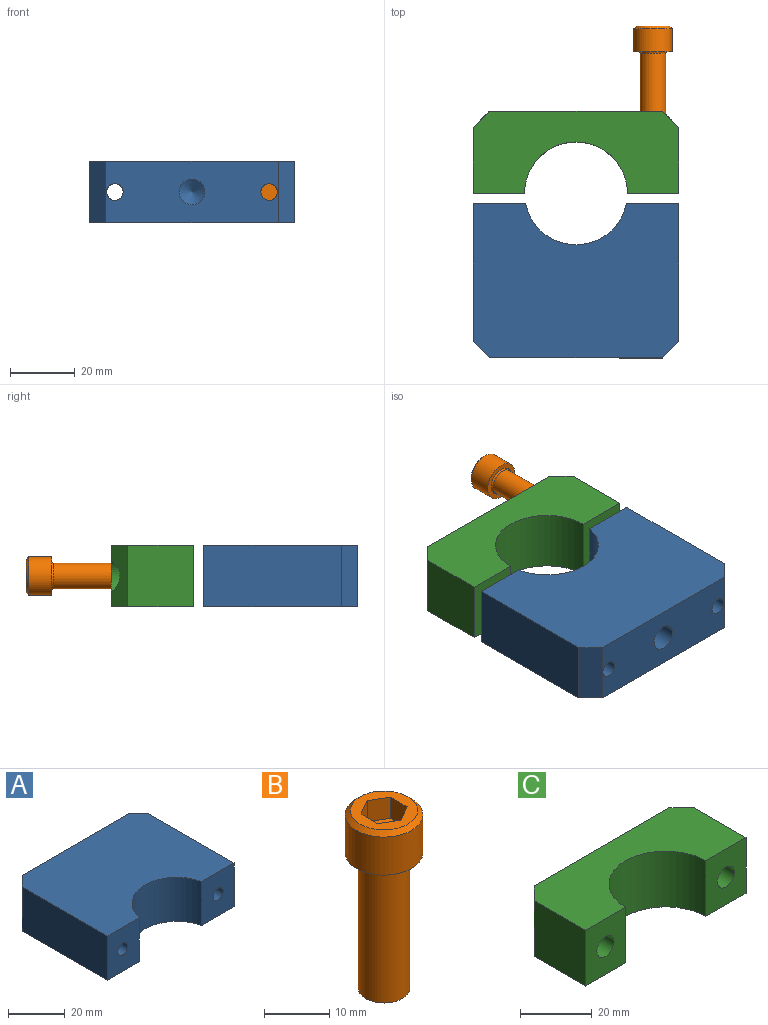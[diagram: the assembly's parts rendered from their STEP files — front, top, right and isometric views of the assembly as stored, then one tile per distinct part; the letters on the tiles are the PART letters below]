
ASSEMBLY  parts=3 mates=3
PART A: 14 faces, bbox 63.5x47.6x19.1 mm
  f0: plane 42.55x19.05mm, normal (1,0,0), area 810.5mm2, adj f3,f4,f9,f11
  f1: plane 42.55x19.05mm, normal (-1,0,0), area 810.5mm2, adj f3,f4,f8,f10
  f2: cylinder r=15.88mm len=31.11mm, axis (0,0,-1), area 828.3mm2, adj f3,f4,f10,f11
  f3: plane 63.5x47.63mm, normal (0,0,1), area 2702.6mm2, adj f0,f1,f2,f7,f8,f9,f10,f11
  f4: plane 63.5x47.63mm, normal (0,0,-1), area 2702.6mm2, adj f0,f1,f2,f7,f8,f9,f10,f11
  f5: cylinder r=2.55mm len=47.63mm, axis (0,1,0), area 763.9mm2, adj f7,f11
  f6: cylinder r=2.55mm len=47.63mm, axis (0,1,0), area 763.9mm2, adj f7,f10
  f7: plane 53.34x19.05mm, normal (0,1,0), area 925.7mm2, adj f3,f4,f5,f6,f8,f9,f12
  f8: plane 19.05x5.08mm, normal (-0.71,0.71,0), area 136.9mm2, adj f1,f3,f4,f7
  f9: plane 19.05x5.08mm, normal (0.71,0.71,0), area 136.9mm2, adj f0,f3,f4,f7
  f10: plane 19.05x16.2mm, normal (0,-1,0), area 288.1mm2, adj f1,f2,f3,f4,f6
  f11: plane 19.05x16.2mm, normal (0,-1,0), area 288.1mm2, adj f0,f2,f3,f4,f5
  f12: cylinder r=3.97mm len=17.48mm, axis (0,1,0), area 435.8mm2, adj f7,f13
  f13: cone r=0mm half-angle=59deg, axis (0,1,0), area 57.7mm2, adj f12
PART B: 14 faces, bbox 11.9x11.9x33.3 mm
  f0: cylinder r=3.97mm len=24.97mm, axis (0,0,-1), area 622.6mm2, adj f1,f5
  f1: plane 7.94x7.94mm, normal (0,0,-1), area 49.5mm2, adj f0
  f2: plane 11.91x11.91mm, normal (0,0,-1), area 50.6mm2, adj f3,f5
  f3: cylinder r=5.96mm len=11.91mm, axis (0,0,-1), area 267.3mm2, adj f2,f13
  f4: plane 10.32x10.32mm, normal (0,0,1), area 48.8mm2, adj f6,f7,f8,f9,f10,f11,f13
  f5: torus R=4.4mm, axis (0,0,1), area 17.6mm2, adj f0,f2
  f6: plane 3.97x3.18mm, normal (0.5,-0.87,0), area 14.6mm2, adj f4,f7,f11,f12
  f7: plane 3.97x3.18mm, normal (-0.5,-0.87,0), area 14.6mm2, adj f4,f6,f8,f12
  f8: plane 3.97x3.67mm, normal (-1,0,0), area 14.6mm2, adj f4,f7,f9,f12
  f9: plane 3.97x3.18mm, normal (-0.5,0.87,0), area 14.6mm2, adj f4,f8,f10,f12
  f10: plane 3.97x3.18mm, normal (0.5,0.87,0), area 14.6mm2, adj f4,f9,f11,f12
  f11: plane 3.97x3.67mm, normal (1,0,0), area 14.6mm2, adj f4,f6,f10,f12
  f12: plane 7.33x6.35mm, normal (0,0,1), area 34.9mm2, adj f6,f7,f8,f9,f10,f11
  f13: cone r=5.16mm half-angle=45deg, axis (0,0,-1), area 39.2mm2, adj f3,f4
PART C: 16 faces, bbox 63.5x25.4x19.1 mm
  f0: plane 19.05x15.88mm, normal (0,-1,0), area 266.6mm2, adj f1,f5,f6,f7,f8
  f1: plane 20.32x19.05mm, normal (1,0,0), area 387.1mm2, adj f0,f6,f7,f15
  f2: plane 53.34x19.05mm, normal (0,1,0), area 858.6mm2, adj f6,f7,f10,f13,f14,f15
  f3: plane 20.32x19.05mm, normal (-1,0,0), area 387.1mm2, adj f4,f6,f7,f14
  f4: plane 19.05x15.88mm, normal (0,-1,0), area 266.6mm2, adj f3,f5,f6,f7,f11
  f5: cylinder r=15.88mm len=31.75mm, axis (0,0,-1), area 950.1mm2, adj f0,f4,f6,f7
  f6: plane 63.5x25.4mm, normal (0,0,1), area 1191.2mm2, adj f0,f1,f2,f3,f4,f5,f14,f15
  f7: plane 63.5x25.4mm, normal (0,0,-1), area 1191.2mm2, adj f0,f1,f2,f3,f4,f5,f14,f15
  f8: cylinder r=3.38mm len=19.05mm, axis (0,1,0), area 404.4mm2, adj f0,f9
  f9: plane 11.11x11.11mm, normal (0,1,0), area 61.1mm2, adj f8,f10
  f10: cylinder r=5.56mm len=11.11mm, axis (0,1,0), area 201.5mm2, adj f2,f9,f15
  f11: cylinder r=3.38mm len=19.05mm, axis (0,1,0), area 404.4mm2, adj f4,f12
  f12: plane 11.11x11.11mm, normal (0,1,0), area 61.1mm2, adj f11,f13
  f13: cylinder r=5.56mm len=11.11mm, axis (0,1,0), area 201.5mm2, adj f2,f12,f14
  f14: plane 19.05x5.08mm, normal (-0.71,0.71,0), area 111.1mm2, adj f2,f3,f6,f7,f13
  f15: plane 19.05x5.08mm, normal (0.71,0.71,0), area 111.1mm2, adj f1,f2,f6,f7,f10
PLACE A rot(axis=(1,0,0),180deg) t=(0,0,19.05)mm
PLACE B rot(axis=(-0.77,-0.45,-0.45),104.9deg) t=(55.56,18.35,9.53)mm
PLACE C at identity fixed
MATE cylindrical C.f11 <-> A.f6  axis (0,1,0) through (7.94,9.52,9.53)mm
MATE cylindrical B.f0 <-> C.f8  axis (0,-1,0) through (55.56,30.84,9.53)mm
MATE cylindrical A.f2 <-> C.f5  axis (0,0,1) through (31.75,0,9.53)mm
